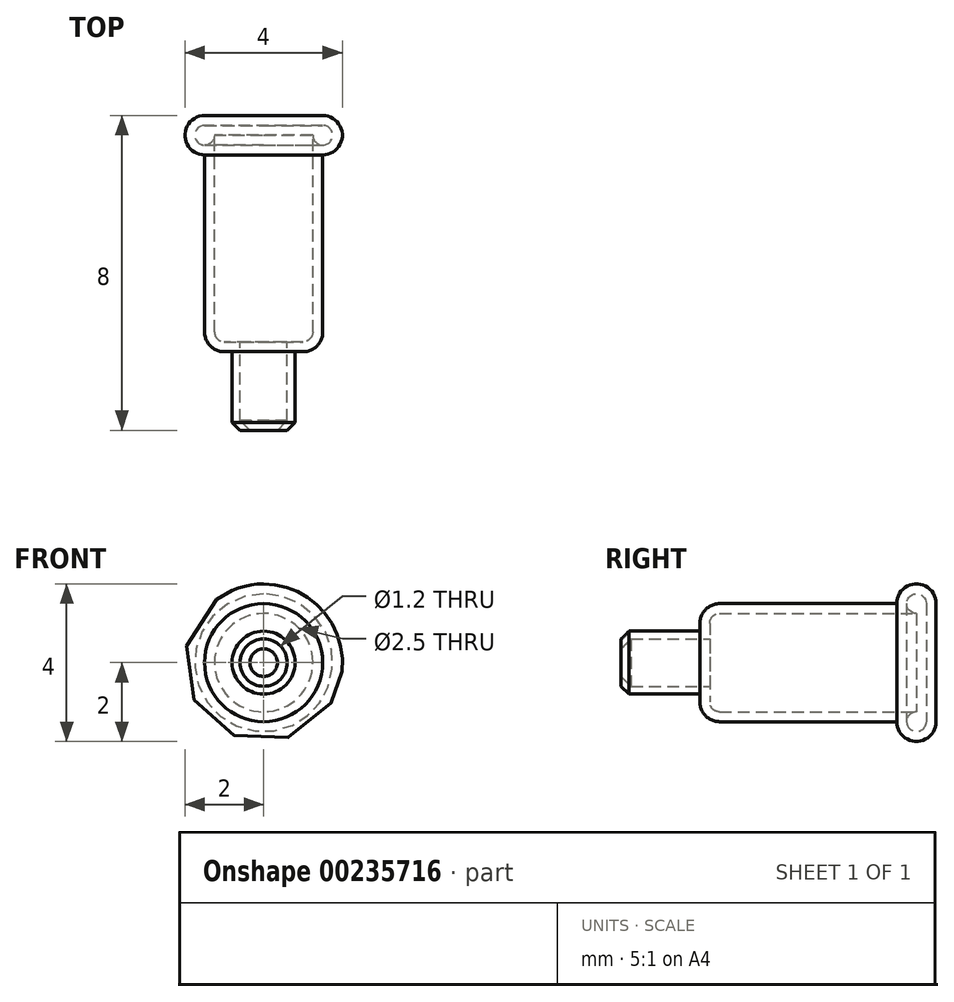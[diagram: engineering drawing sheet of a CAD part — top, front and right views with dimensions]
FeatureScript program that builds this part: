
annotation { "Feature Type Name" : "Feature", "Feature Type Description" : "" }
export const myFeature = defineFeature(function(context is Context, id is Id, definition is map)
    precondition{}
    {
        {
            var Q0;
            Q0=qCreatedBy(makeId("Top.planeOp"),FACE);
            var sketch = newSketch(context, id + "F0", { "sketchPlane" : qUnion([Q0])});
            skLineSegment(sketch, "E0", {"start": v(0, 0) * mm, "end": v(0, 8) * mm});
            skLineSegment(sketch, "E1.bottom", {"start": v(0, 0) * mm, "end": v(-0.6, 0) * mm});
            skLineSegment(sketch, "E1.top", {"start": v(0, 2) * mm, "end": v(-0.6, 2) * mm});
            skLineSegment(sketch, "E1.left", {"start": v(0, 0) * mm, "end": v(0, 2) * mm});
            skLineSegment(sketch, "E1.right", {"start": v(-0.8, 0.2) * mm, "end": v(-0.8, 2) * mm});
            skLineSegment(sketch, "E2.top", {"start": v(0, 7) * mm, "end": v(-1.25, 7) * mm});
            skLineSegment(sketch, "E2.left", {"start": v(0, 2) * mm, "end": v(0, 7) * mm});
            skLineSegment(sketch, "E2.right", {"start": v(-1.5, 2.5) * mm, "end": v(-1.5, 7) * mm});
            skLineSegment(sketch, "E3.top", {"start": v(0, 8) * mm, "end": v(-1.5, 8) * mm});
            skLineSegment(sketch, "E3.left", {"start": v(0, 7) * mm, "end": v(0, 8) * mm});
            skLineSegment(sketch, "E3.right", {"start": v(-2, 7.5) * mm, "end": v(-2, 7.5) * mm});
            skPoint(sketch, "E4.visualSharp", {"position": v(-2, 8) * mm});
            skArc(sketch, "E5.filletArc", {"start": v(-1.5, 8) * mm, "mid": v(-1.85, 7.85) * mm, "end": v(-2, 7.5) * mm});
            skPoint(sketch, "E6.visualSharp", {"position": v(-2, 7) * mm});
            skArc(sketch, "E6.filletArc", {"start": v(-2, 7.5) * mm, "mid": v(-1.85, 7.15) * mm, "end": v(-1.5, 7) * mm});
            skPoint(sketch, "E7.visualSharp", {"position": v(-1.5, 2) * mm});
            skArc(sketch, "E7.filletArc", {"start": v(-1.5, 2.5) * mm, "mid": v(-1.35, 2.15) * mm, "end": v(-1, 2) * mm});
            skLineSegment(sketch, "E8", {"start": v(-0.8, 0.2) * mm, "end": v(-0.6, 0) * mm});
            skLineSegment(sketch, "E9", {"start": v(0, 8) * mm, "end": v(0, 0) * mm});
            skLineSegment(sketch, "E10", {"start": v(0, 8.9) * mm, "end": v(0, -0.62) * mm});
            skLineSegment(sketch, "E11", {"start": v(-0.6, 0) * mm, "end": v(-0.35, 0) * mm});
            skLineSegment(sketch, "E12", {"start": v(-0.35, 0) * mm, "end": v(-0.6, 0.25) * mm});
            skLineSegment(sketch, "E13", {"start": v(-0.6, 0.25) * mm, "end": v(-0.6, 2) * mm});
            skLineSegment(sketch, "E14", {"start": v(-0.6, 2) * mm, "end": v(-0.6, 2.25) * mm});
            skLineSegment(sketch, "E15", {"start": v(-1.25, 7) * mm, "end": v(-1.25, 7.5) * mm});
            skArc(sketch, "E16", {"start": v(-1.5, 7.75) * mm, "mid": v(-1.68, 7.32) * mm, "end": v(-1.25, 7.5) * mm});
            skLineSegment(sketch, "E17", {"start": v(-1.5, 7.75) * mm, "end": v(0, 7.75) * mm});
            skPoint(sketch, "E18.visualSharp", {"position": v(-1.25, 2.25) * mm});
            skLineSegment(sketch, "E19", {"start": v(-1.25, 7.5) * mm, "end": v(0, 7.5) * mm});
            skLineSegment(sketch, "E20.trimOffspring", {"start": v(-0.8, 2) * mm, "end": v(-1, 2) * mm});
            skArc(sketch, "E21.0", {"start": v(-1.25, 2.5) * mm, "mid": v(-1.18, 2.32) * mm, "end": v(-1, 2.25) * mm});
            skLineSegment(sketch, "E22", {"start": v(-1.25, 7) * mm, "end": v(-1.25, 2.5) * mm});
            skLineSegment(sketch, "E23", {"start": v(-1, 2.25) * mm, "end": v(-0.6, 2.25) * mm});
            skSolve(sketch);
        }
        {
            var Q0;
            Q0=makeQuery(id+"F0.imprint","IMPRINT",FACE,{"disambiguationData":[TD([[makeQuery(id+"F0.imprint","IMPRINT",EDGE,{"derivedFrom":sQuery(id+"F0.wireOp",EDGE,"E1.right")}),-1.0]])]});
            var Q1;
            Q1=sQuery(id+"F0.wireOp",EDGE,"E10");
            revolve(context, id + "F1", {"entities" : qUnion([Q0]), "axis" : qUnion([Q1]), "revolveType" : RevolveType.FULL});
        }
    });
